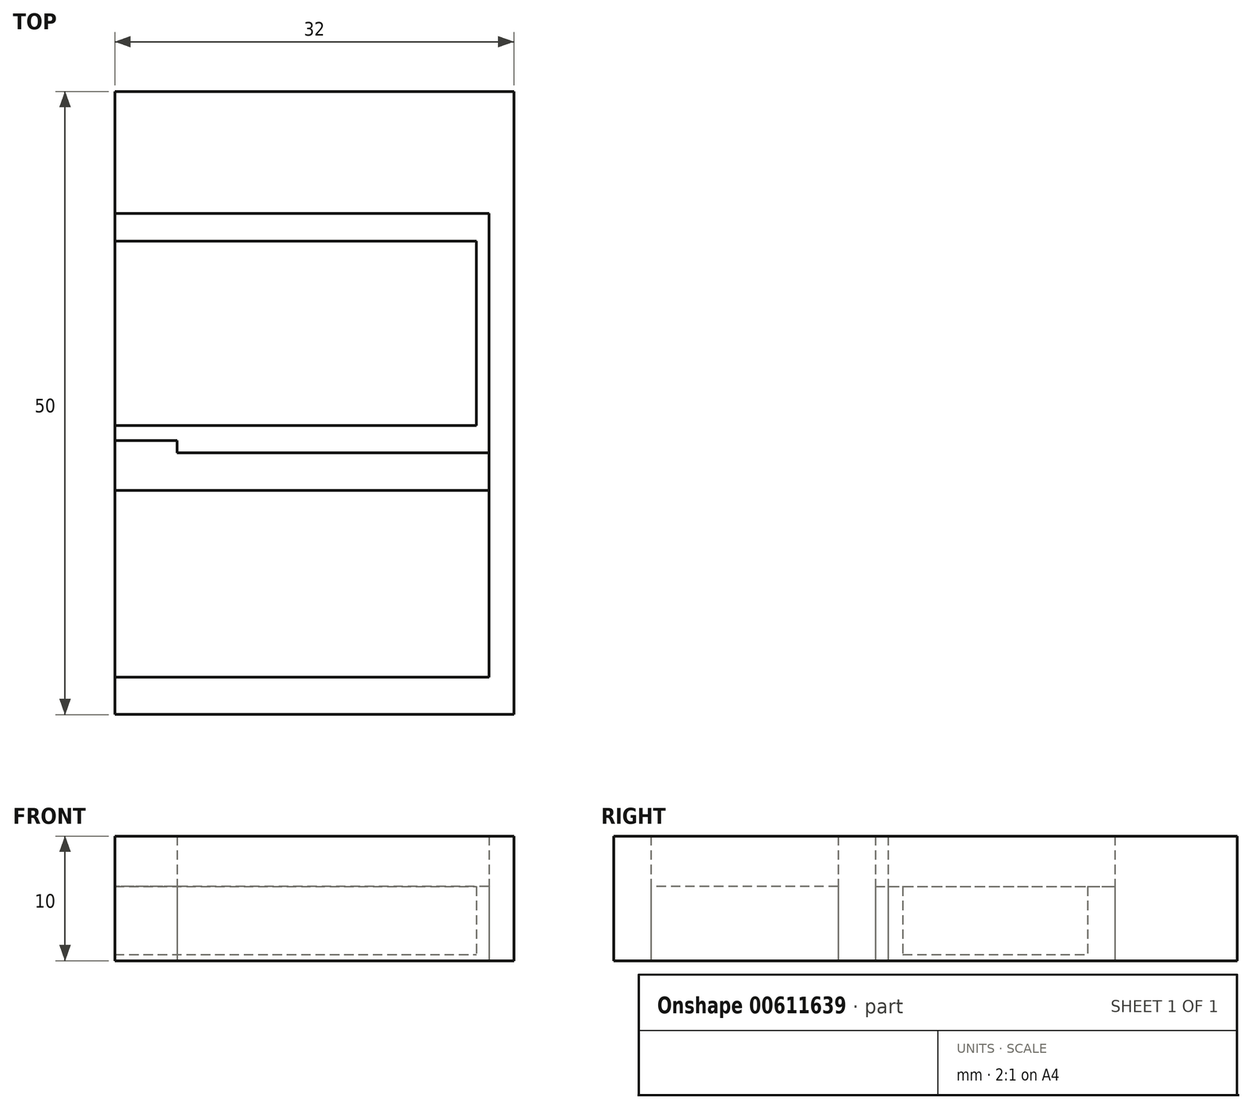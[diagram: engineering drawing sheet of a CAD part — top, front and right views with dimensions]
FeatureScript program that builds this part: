
annotation { "Feature Type Name" : "Feature", "Feature Type Description" : "" }
export const myFeature = defineFeature(function(context is Context, id is Id, definition is map)
    precondition{}
    {
        {
            var Q0;
            Q0=qCreatedBy(makeId("Top.planeOp"),FACE);
            var sketch = newSketch(context, id + "F0", { "sketchPlane" : qUnion([Q0])});
            skLineSegment(sketch, "E0.bottom", {"start": v(-8.5, 23.2) * mm, "end": v(23.5, 23.2) * mm});
            skLineSegment(sketch, "E0.top", {"start": v(-8.5, -26.8) * mm, "end": v(23.5, -26.8) * mm});
            skLineSegment(sketch, "E0.right", {"start": v(23.5, 23.2) * mm, "end": v(23.5, -26.8) * mm});
            skLineSegment(sketch, "E1", {"start": v(-1.5, -26.8) * mm, "end": v(-1.5, -23.8) * mm, "construction": true});
            skLineSegment(sketch, "E2", {"start": v(23.5, -20.8) * mm, "end": v(21.5, -20.8) * mm, "construction": true});
            skLineSegment(sketch, "E3", {"start": v(21.5, -23.8) * mm, "end": v(21.5, -8.8) * mm});
            skLineSegment(sketch, "E4", {"start": v(21.5, -8.8) * mm, "end": v(21.5, -5.8) * mm});
            skLineSegment(sketch, "E5", {"start": v(21.5, -5.8) * mm, "end": v(-3.5, -5.8) * mm});
            skLineSegment(sketch, "E6", {"start": v(-3.5, -5.8) * mm, "end": v(-3.5, -4.8) * mm});
            skLineSegment(sketch, "E7", {"start": v(-3.5, -4.8) * mm, "end": v(-8.5, -4.8) * mm});
            skLineSegment(sketch, "E8", {"start": v(-8.5, -4.8) * mm, "end": v(-8.5, 13.4) * mm});
            skLineSegment(sketch, "E9", {"start": v(-8.5, 13.4) * mm, "end": v(-3.5, 13.4) * mm});
            skLineSegment(sketch, "E10", {"start": v(-3.5, 13.4) * mm, "end": v(-3.5, 14.4) * mm});
            skLineSegment(sketch, "E11", {"start": v(9, -5.8) * mm, "end": v(9, -3.6) * mm, "construction": true});
            skPoint(sketch, "E11.endSnap0", {"position": v(9, -5.8) * mm});
            skLineSegment(sketch, "E12", {"start": v(21.5, 13.4) * mm, "end": v(-3.5, 13.4) * mm});
            skLineSegment(sketch, "E13", {"start": v(21.5, -5.8) * mm, "end": v(21.5, 13.4) * mm});
            skLineSegment(sketch, "E14", {"start": v(21.5, 3.8) * mm, "end": v(20.5, 3.8) * mm, "construction": true});
            skPoint(sketch, "E14.endSnap0", {"position": v(21.5, 3.8) * mm});
            skLineSegment(sketch, "E15", {"start": v(9, 13.4) * mm, "end": v(9, 11.2) * mm, "construction": true});
            skLineSegment(sketch, "E16", {"start": v(-8.5, -3.6) * mm, "end": v(20.5, -3.6) * mm});
            skLineSegment(sketch, "E17", {"start": v(20.5, -3.6) * mm, "end": v(20.5, 11.2) * mm});
            skLineSegment(sketch, "E18", {"start": v(20.5, 11.2) * mm, "end": v(-8.5, 11.2) * mm});
            skLineSegment(sketch, "E19", {"start": v(-8.5, -4.8) * mm, "end": v(-8.5, -26.8) * mm});
            skLineSegment(sketch, "E20", {"start": v(21.5, -8.8) * mm, "end": v(-8.5, -8.8) * mm});
            skLineSegment(sketch, "E21", {"start": v(-8.5, -23.8) * mm, "end": v(21.5, -23.8) * mm});
            skPoint(sketch, "E0.left.end.orphan", {"position": v(-26.5, -26.8) * mm});
            skLineSegment(sketch, "E22", {"start": v(-8.5, 13.4) * mm, "end": v(-8.5, 23.2) * mm});
            skSolve(sketch);
        }
        {
            var Q0;
            {var subQ0=sQuery(id+"F0.wireOp",EDGE,"E16");Q0=makeQuery(id+"F0.imprint","IMPRINT",FACE,{"disambiguationData":[TD([[makeQuery(id+"F0.imprint","IMPRINT",EDGE,{"derivedFrom":subQ0}),1.0]])]});}
            extrude(context, id + "F1", {"entities" : qUnion([Q0]), "depth" : .5 * mm, "offsetDistance" : 25 * mm});
        }
        {
            var Q0;
            Q0=makeQuery(id+"F0.imprint","IMPRINT",FACE,{"disambiguationData":[TD([[makeQuery(id+"F0.imprint","IMPRINT",EDGE,{"derivedFrom":sQuery(id+"F0.wireOp",EDGE,"E5")}),-1.0]])]});
            extrude(context, id + "F2", {"entities" : qUnion([Q0]), "operationType" : NewBodyOperationType.ADD, "depth" : 5.95 * mm, "offsetDistance" : 25 * mm});
        }
        {
            var Q0;
            {var subQ4=sQuery(id+"F0.wireOp",EDGE,"E3");Q0=makeQuery(id+"F0.imprint","IMPRINT",FACE,{"disambiguationData":[TD([[makeQuery(id+"F0.imprint","IMPRINT",EDGE,{"derivedFrom":subQ4}),1.0]])]});}
            extrude(context, id + "F3", {"entities" : qUnion([Q0]), "depth" : 5.95 * mm, "offsetDistance" : 25 * mm});
        }
        {
            var Q0;
            {var subQ5=sQuery(id+"F0.wireOp",EDGE,"E0.bottom");Q0=makeQuery(id+"F0.imprint","IMPRINT",FACE,{"disambiguationData":[TD([[makeQuery(id+"F0.imprint","IMPRINT",EDGE,{"derivedFrom":subQ5}),-1.0]])]});}
            var Q1;
            {var subQ4=sQuery(id+"F0.wireOp",EDGE,"E0.top");Q1=makeQuery(id+"F0.imprint","IMPRINT",FACE,{"disambiguationData":[TD([[makeQuery(id+"F0.imprint","IMPRINT",EDGE,{"derivedFrom":subQ4}),1.0]])]});}
            extrude(context, id + "F4", {"entities" : qUnion([Q0, Q1]), "depth" : 10 * mm, "offsetDistance" : 25 * mm});
        }
        {
            var Q0;
            Q0=makeQuery(id+"F0.imprint","IMPRINT",FACE,{"disambiguationData":[TD([[makeQuery(id+"F0.imprint","IMPRINT",EDGE,{"derivedFrom":sQuery(id+"F0.wireOp",EDGE,"E4")}),1.0]])]});
            extrude(context, id + "F5", {"entities" : qUnion([Q0]), "depth" : 10 * mm, "offsetDistance" : 25 * mm});
        }
    });
